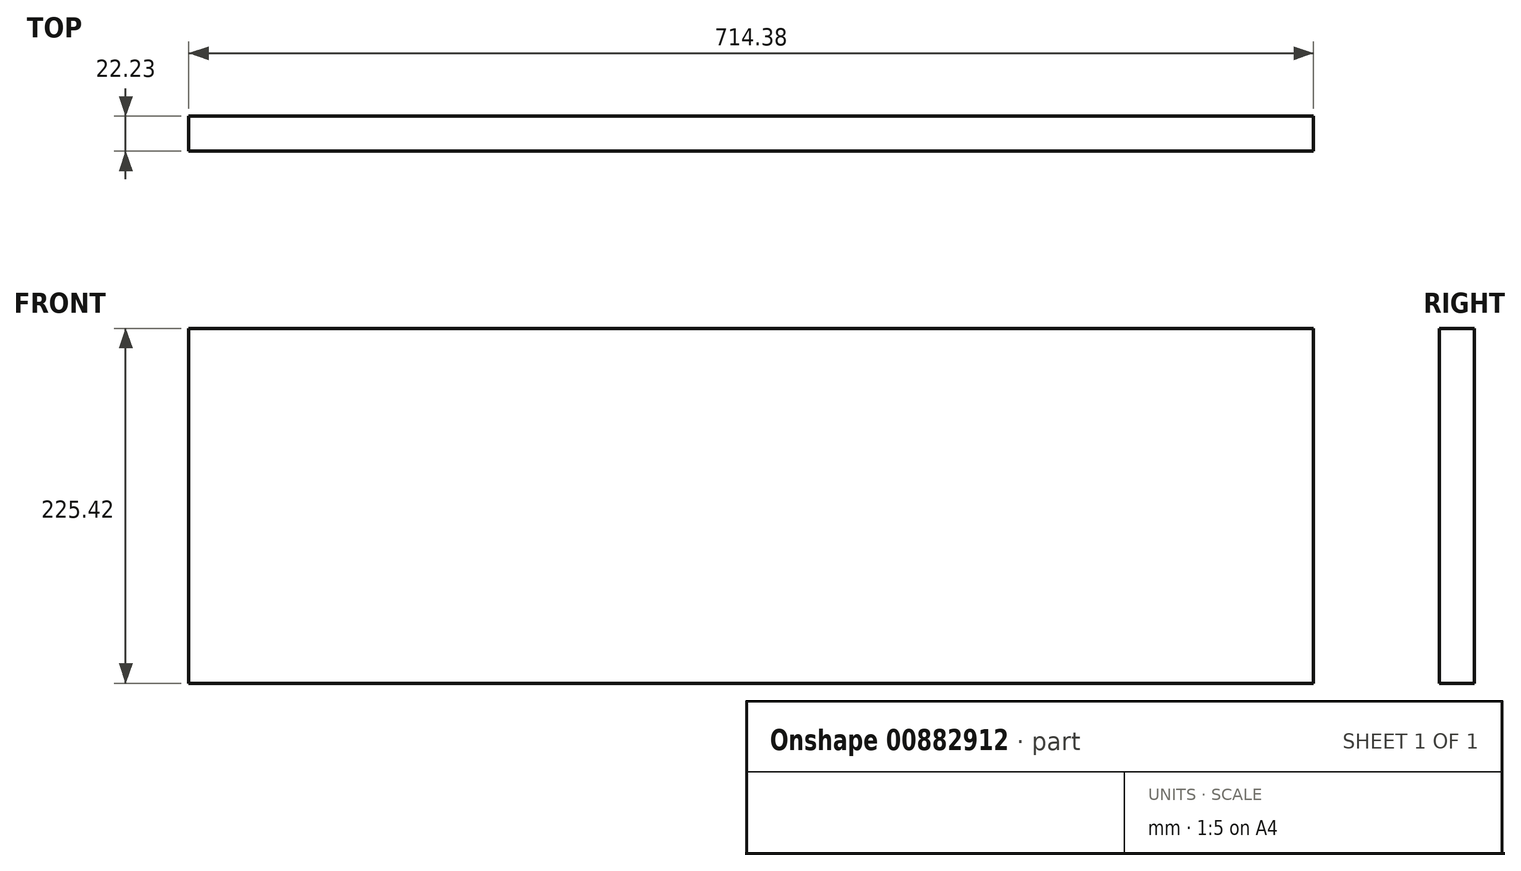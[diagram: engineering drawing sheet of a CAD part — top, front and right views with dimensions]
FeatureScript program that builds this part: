
annotation { "Feature Type Name" : "Feature", "Feature Type Description" : "" }
export const myFeature = defineFeature(function(context is Context, id is Id, definition is map)
    precondition{}
    {
        {
            var Q0;
            Q0=qCreatedBy(makeId("Front.planeOp"),FACE);
            var sketch = newSketch(context, id + "F0", { "sketchPlane" : qUnion([Q0])});
            skLineSegment(sketch, "E0.bottom", {"start": v(0, 0) * mm, "end": v(714.38, 0) * mm});
            skLineSegment(sketch, "E0.top", {"start": v(0, -225.42) * mm, "end": v(714.38, -225.42) * mm});
            skLineSegment(sketch, "E0.left", {"start": v(0, 0) * mm, "end": v(0, -225.42) * mm});
            skLineSegment(sketch, "E0.right", {"start": v(714.38, 0) * mm, "end": v(714.38, -225.42) * mm});
            skSolve(sketch);
        }
        {
            var Q0;
            Q0=makeQuery(id+"F0.imprint","IMPRINT",FACE,{"disambiguationData":[TD([[makeQuery(id+"F0.imprint","IMPRINT",EDGE,{"derivedFrom":sQuery(id+"F0.wireOp",EDGE,"E0.bottom")}),-1.0]])]});
            extrude(context, id + "F1", {"entities" : qUnion([Q0]), "depth" : 22.22 * mm, "offsetDistance" : 25.4 * mm});
        }
    });
